# Revit family: Power-ModularDevices-GEWISS-90AM-SWITCH_DISCONNECTOR_4P
name_source: partatom
category: Apparecchi elettrici
revit_build: Autodesk Revit 2016 (Build: 20161004_0715(x64)
units: mm (PartAtom-declared; Revit-internal decimal feet)

## family parameters
Condiviso = No
Host = Superficie
Mantenere orientamento annotazione = Sì
Numero OmniClass = 23.80.50.00
Punto di calcolo locali = Sì
Quota connettore circolare = Usa diametro
Taglio con vuoti quando caricato = No
Tipo di parte = Normale
Titolo OmniClass = Terminals for Power Supply

## types (6) — shared parameters
Catalogue = POWER
Catalogue Range = 90 AM
Electrocod = 1422
IDF = 430158d9-1433-4288-b99a-0bbaab83fd28
IDT = fdf7da26-c6e5-4906-8e65-8ea3b9be747a
Immagine tipo = GW96134.jpg
No. Chorus modules = 4
No. of modules EN 50022 = 4
No. of poles = 4P
Number of poles = 4P
Numero di poli = 3
Produttore = GEWISS S.p.A.
Prospetto di default = 1219 mm
Rated voltage = 415Vac
Rated voltage AC = 415V
SEO = Disconnector
Spostamento_x = -340 mm
Standard = EN 60947-3
Technical sheet = https://www.gewiss.com
URL = https://www.gewiss.com
Version file RFA = 18.0
carico = Altro
potenza in watt = 0 V

## per-type parameters (varying)
| type | Descrizione | EAN code | Modello | Rated current (In) | Rated current: |
| GW96177 - SWITCH DISCONNECTOR 4P 80A | SWITCH DISCONNECTOR 4P 80A | 8011564131750 | GW96177 | 80A | 80A |
| GW96135 - SWITCH DISCONNECTOR 4P 40A | SWITCH DISCONNECTOR 4P 40A | 8011564110465 | GW96135 | 40A | 40A |
| GW96134 - SWITCH DISCONNECTOR 4P 32A | SWITCH DISCONNECTOR 4P 32A | 8011564110458 | GW96134 | 32A | 32A |
| GW96176 - SWITCH DISCONNECTOR 4P 63A | SWITCH DISCONNECTOR 4P 63A | 8011564131743 | GW96176 | 63A | 63A |
| GW96179 - SWITCH DISCONNECTOR 4P 125A | SWITCH DISCONNECTOR 4P 125A | 8011564131774 | GW96179 | 125A | 125A |
| GW96178 - SWITCH DISCONNECTOR 4P 100A | SWITCH DISCONNECTOR 4P 100A | 8011564131767 | GW96178 | 100A | 100A |
